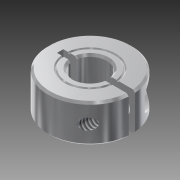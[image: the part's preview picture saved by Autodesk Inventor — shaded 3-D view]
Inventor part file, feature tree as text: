
AUTODESK INVENTOR PART (.ipt)
format: ipt  version: 2016 SP1 (Build 200210100, 210)  size: 407,040 bytes
history: native  units: mm
features: sketch x3, hole x2, other x2, surface_op x1, thread x1, extrude x1, projected_geometry x1
ambient origin geometry x8: Origin, YZ Plane, XZ Plane, XY Plane, X Axis, Y Axis, Z Axis, Center Point
bodies: Solid1 (feature_tree)
feature tree (11):
  surface_op  "Stitch Surface1"
  thread  "Thread1"  [1 undecoded]
  hole  "Hole1"  [1 undecoded]
  extrude  "Extrusion1"  [1 undecoded]
  hole  "Hole2"  [1 undecoded]
  sketch  "Sketch2"  dims[d2=3.264mm d3=6.0mm d4=9.525mm d5=1.524mm d6=14.3117mm d7=8.0mm d8=20.594885mm d9=10.0mm d10=0.0mm]
  sketch  "Sketch3"  dims[d11=2.156mm d12=6.0mm d13=9.525mm d14=1.524mm d15=14.3117mm d16=8.0mm d17=20.594885mm]
  sketch  "Sketch4"
  projected_geometry  "Projected Loop1"
  other  "Composite1"
  other  "Srf1"
note: 4 required parameter values undecoded (feature->parameter linkage not recoverable at this tier; creation-order binding heuristic only, values carry confidence <= 0.55)
